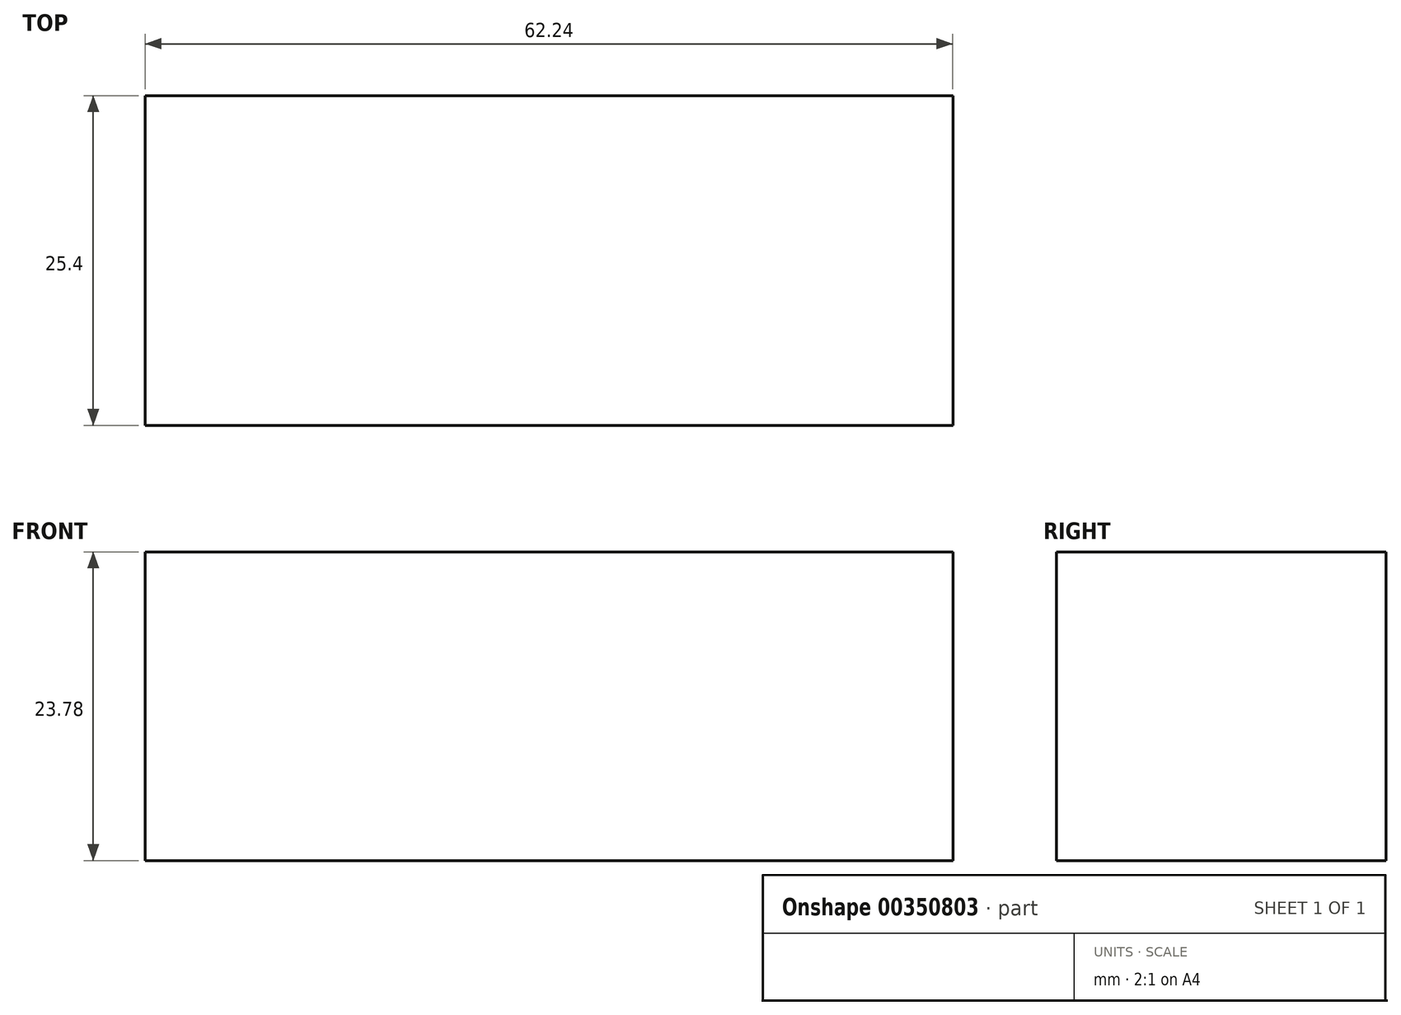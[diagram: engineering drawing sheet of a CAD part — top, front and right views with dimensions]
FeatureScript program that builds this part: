
annotation { "Feature Type Name" : "Feature", "Feature Type Description" : "" }
export const myFeature = defineFeature(function(context is Context, id is Id, definition is map)
    precondition{}
    {
        {
            var Q0;
            Q0=qCreatedBy(makeId("Front.planeOp"),FACE);
            var sketch = newSketch(context, id + "F0", { "sketchPlane" : qUnion([Q0])});
            skLineSegment(sketch, "E0.bottom", {"start": v(31.12, 11.9) * mm, "end": v(-31.12, 11.9) * mm});
            skLineSegment(sketch, "E0.top", {"start": v(31.12, -11.9) * mm, "end": v(-31.12, -11.9) * mm});
            skLineSegment(sketch, "E0.left", {"start": v(31.12, 11.9) * mm, "end": v(31.12, -11.9) * mm});
            skLineSegment(sketch, "E0.right", {"start": v(-31.12, 11.9) * mm, "end": v(-31.12, -11.9) * mm});
            skPoint(sketch, "E0.middle", {"position": v(0, 0) * mm});
            skSolve(sketch);
        }
        {
            var Q0;
            Q0=makeQuery(id+"F0.imprint","IMPRINT",FACE,{"disambiguationData":[TD([[makeQuery(id+"F0.imprint","IMPRINT",EDGE,{"derivedFrom":sQuery(id+"F0.wireOp",EDGE,"E0.bottom")}),1.0]])]});
            extrude(context, id + "F1", {"entities" : qUnion([Q0]), "depth" : 25.4 * mm});
        }
    });
